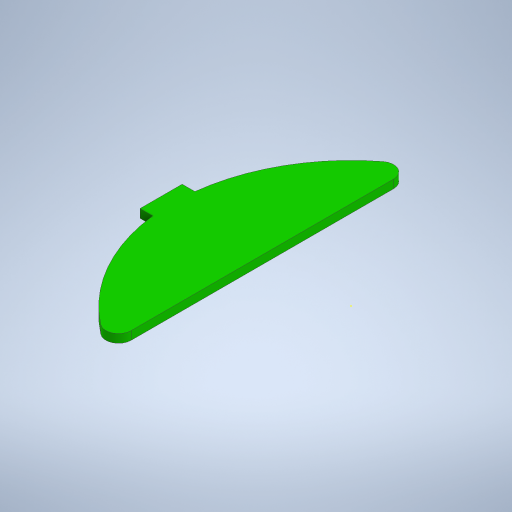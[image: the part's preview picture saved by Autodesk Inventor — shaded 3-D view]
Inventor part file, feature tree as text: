
AUTODESK INVENTOR PART (.ipt)
format: ipt  version: 2024 (Build 280153000, 153)  size: 241,664 bytes
history: native  units: mm
features: sketch x2, extrude x1, fillet x1
ambient origin geometry x8: Origin, YZ Plane, XZ Plane, XY Plane, X Axis, Y Axis, Z Axis, Center Point
bodies: Solide1 (feature_tree)
feature tree (4):
  extrude  "Extrusion1"  Depth=2.0mm TaperAngle=0.0deg
  fillet  "Congé2"  Radius=3.0mm
  sketch  "Esquisse2"
  sketch  "Esquisse1"
